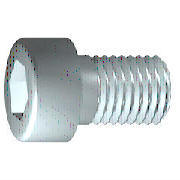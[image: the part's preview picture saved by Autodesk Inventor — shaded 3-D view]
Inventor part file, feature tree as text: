
AUTODESK INVENTOR PART (.ipt)
format: ipt  version: 2022 (Build 260153000, 153)  size: 186,368 bytes
history: native  units: mm (DEFAULTED — no unit token found)
features: sketch x2, extrude x1, plane x1, fillet x1
ambient origin geometry x7: Origin, YZ Plane, XY Plane, X Axis, Y Axis, Z Axis, Center Point
bodies: Solid1 (feature_tree), Body (feature_tree)
feature tree (5):
  extrude  "Slot"  Depth=10.0mm
  plane  "Work Plane1"
  fillet  "Fillet2"  Radius=10.0mm
  sketch  "Sketch1"  dims[d1=32.0mm d2=0.920275mm d3=10.0mm]
  sketch  "Sketch2"  dims[d4=5.0mm d5=60.0deg d6=10.0mm d7=10.0mm d8=9.237604mm d9=16.0mm d10=90.0deg d11=10.0mm d12=0.0mm d13=32.0mm d14=0.0mm d15=0.920175mm d16=0.920175mm d17=1.0mm d19=0.0mm d26=80.0mm d27=45.0deg d28=0.0mm d29=0.0mm d30=0.1mm]
